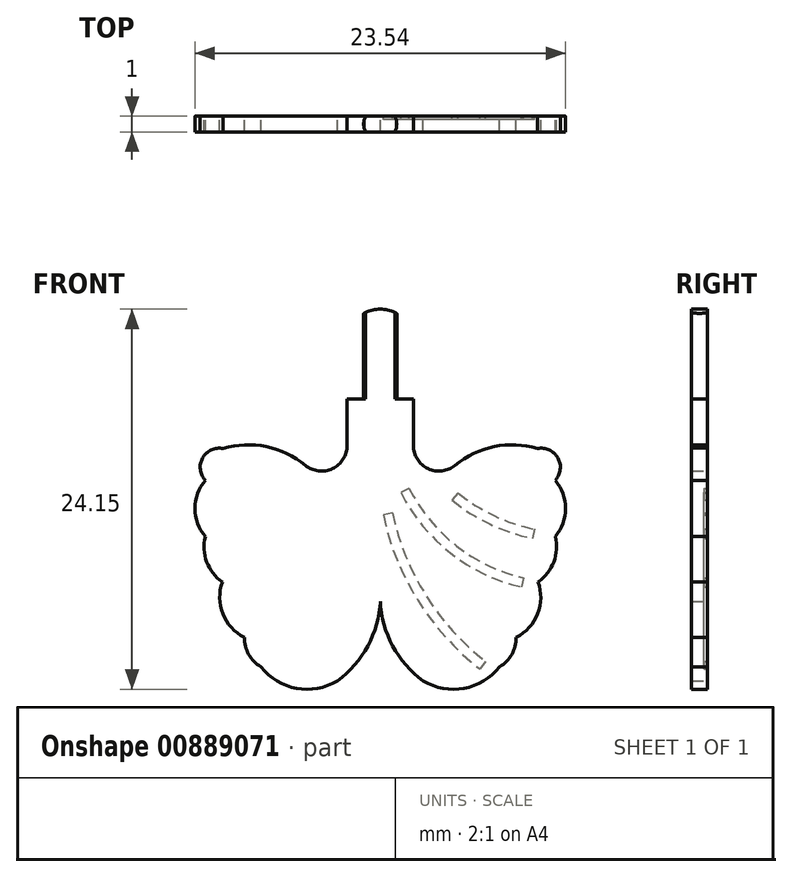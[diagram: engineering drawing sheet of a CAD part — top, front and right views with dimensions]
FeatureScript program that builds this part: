
annotation { "Feature Type Name" : "Feature", "Feature Type Description" : "" }
export const myFeature = defineFeature(function(context is Context, id is Id, definition is map)
    precondition{}
    {
        {
            var Q0;
            Q0=qCreatedBy(makeId("Front.planeOp"),FACE);
            var sketch = newSketch(context, id + "F0", { "sketchPlane" : qUnion([Q0])});
            skLineSegment(sketch, "E0", {"start": v(0, 4.31) * mm, "end": v(0, 0) * mm, "construction": true});
            skLineSegment(sketch, "E1", {"start": v(6, 0) * mm, "end": v(0, 0) * mm, "construction": true});
            skLineSegment(sketch, "E2", {"start": v(1.05, 6.95) * mm, "end": v(1.05, 3.67) * mm});
            skArc(sketch, "E3", {"start": v(0, -1.28) * mm, "mid": v(0.4, -2.7) * mm, "end": v(1.36, -3.8) * mm});
            skArc(sketch, "E4", {"start": v(1.36, -3.8) * mm, "mid": v(2.66, -4.05) * mm, "end": v(3.79, -3.36) * mm});
            skArc(sketch, "E5", {"start": v(3.79, -3.36) * mm, "mid": v(4.18, -2.97) * mm, "end": v(4.31, -2.43) * mm});
            skArc(sketch, "E6", {"start": v(4.31, -2.43) * mm, "mid": v(5, -1.68) * mm, "end": v(5.01, -0.66) * mm});
            skArc(sketch, "E7", {"start": v(5.01, -0.66) * mm, "mid": v(5.51, -0.03) * mm, "end": v(5.56, 0.77) * mm});
            skArc(sketch, "E8", {"start": v(5.56, 0.77) * mm, "mid": v(5.88, 1.67) * mm, "end": v(5.56, 2.56) * mm});
            skArc(sketch, "E9", {"start": v(1.05, 3.67) * mm, "mid": v(1.52, 2.93) * mm, "end": v(2.38, 3.04) * mm});
            skArc(sketch, "E10", {"start": v(5.56, 2.56) * mm, "mid": v(5.64, 3.27) * mm, "end": v(5, 3.57) * mm});
            skArc(sketch, "E11", {"start": v(5, 3.57) * mm, "mid": v(3.62, 3.63) * mm, "end": v(2.38, 3.04) * mm});
            skLineSegment(sketch, "E12.left", {"start": v(1.05, 6.95) * mm, "end": v(1.05, 6.95) * mm});
            skLineSegment(sketch, "E12.right", {"start": v(0, 6.95) * mm, "end": v(0, 6.95) * mm});
            skLineSegment(sketch, "E13.bottom", {"start": v(0, -1.28) * mm, "end": v(0, -1.28) * mm});
            skLineSegment(sketch, "E13.left", {"start": v(0, -1.28) * mm, "end": v(0, 8) * mm});
            skLineSegment(sketch, "E13.right", {"start": v(0, -1.28) * mm, "end": v(0, 6.95) * mm});
            skArc(sketch, "E14", {"start": v(1.05, 6.95) * mm, "mid": v(0.74, 7.7) * mm, "end": v(0, 8) * mm});
            skSolve(sketch);
        }
        {
            var Q0;
            Q0=makeQuery(id+"F0.imprint","IMPRINT",FACE,{"disambiguationData":[TD([[makeQuery(id+"F0.imprint","IMPRINT",EDGE,{"derivedFrom":sQuery(id+"F0.wireOp",EDGE,"E2")}),-1.0]])]});
            extrude(context, id + "F1", {"entities" : qUnion([Q0]), "depth" : .25 * mm, "offsetDistance" : 25 * mm, "hasSecondDirection" : true, "secondDirectionOppositeDirection" : true, "secondDirectionDepth" : .25 * mm});
        }
        {
            var Q0;
            Q0=makeQuery(id+"F1.opExtrude","SWEPT_BODY",BODY,{"disambiguationData":[OSD([sQuery(id+"F0.wireOp",EDGE,"E2"),sQuery(id+"F0.wireOp",EDGE,"E3"),sQuery(id+"F0.wireOp",EDGE,"E4"),sQuery(id+"F0.wireOp",EDGE,"E5"),sQuery(id+"F0.wireOp",EDGE,"E6"),sQuery(id+"F0.wireOp",EDGE,"E7"),sQuery(id+"F0.wireOp",EDGE,"E8"),sQuery(id+"F0.wireOp",EDGE,"E9"),sQuery(id+"F0.wireOp",EDGE,"E10"),sQuery(id+"F0.wireOp",EDGE,"E11"),sQuery(id+"F0.wireOp",EDGE,"E13.left"),sQuery(id+"F0.wireOp",EDGE,"E13.right"),sQuery(id+"F0.wireOp",EDGE,"E14")])]});
            var Q1;
            Q1=makeQuery(id+"F1.opExtrude","SWEPT_FACE",FACE,{"disambiguationData":[OSD([sQuery(id+"F0.wireOp",EDGE,"E13.left"),sQuery(id+"F0.wireOp",EDGE,"E13.right")])]});
            mirror(context, id + "F2", {"operationType" : NewBodyOperationType.ADD, "entities" : qUnion([Q0]), "mirrorPlane" : qUnion([Q1])});
        }
        {
            var Q0;
            Q0=qCreatedBy(makeId("Top.planeOp"),FACE);
            cPlane(context, id + "F3", {"entities" : qUnion([Q0]), "cplaneType" : CPlaneType.OFFSET, "offset" : 20 * mm, "width" : 150 * mm, "height" : 150 * mm});
        }
        {
            var Q0;
            Q0=qCreatedBy(id+"F3.planeOp",FACE);
            var sketch = newSketch(context, id + "F4", { "sketchPlane" : qUnion([Q0])});
            skCircle(sketch, "E15", {"center": v(0, 0) * mm, "radius": 1.05 * mm});
            skCircle(sketch, "E16", {"center": v(0, 0) * mm, "radius": 3 * mm});
            skSolve(sketch);
        }
        {
            var Q0;
            {var subQ0=makeQuery(id+"F1.opExtrude","CAP_FACE",FACE,{"disambiguationData":[OSD([sQuery(id+"F0.wireOp",EDGE,"E2"),sQuery(id+"F0.wireOp",EDGE,"E3"),sQuery(id+"F0.wireOp",EDGE,"E4"),sQuery(id+"F0.wireOp",EDGE,"E5"),sQuery(id+"F0.wireOp",EDGE,"E6"),sQuery(id+"F0.wireOp",EDGE,"E7"),sQuery(id+"F0.wireOp",EDGE,"E8"),sQuery(id+"F0.wireOp",EDGE,"E9"),sQuery(id+"F0.wireOp",EDGE,"E10"),sQuery(id+"F0.wireOp",EDGE,"E11"),sQuery(id+"F0.wireOp",EDGE,"E13.left"),sQuery(id+"F0.wireOp",EDGE,"E13.right"),sQuery(id+"F0.wireOp",EDGE,"E14")])],"isStart":true});Q0=makeQuery(id+"F2.boolean.opBoolean","MERGE",FACE,{"derivedFrom":[subQ0,makeQuery(id+"F2.opPattern","COPY",FACE,{"derivedFrom":subQ0,"instanceName":"1"})]});}
            var sketch = newSketch(context, id + "F5", { "sketchPlane" : qUnion([Q0])});
            skArc(sketch, "E17", {"start": v(-3.34, -3.19) * mm, "mid": v(-1.45, -1.1) * mm, "end": v(-0.39, 1.52) * mm});
            skArc(sketch, "E18", {"start": v(-4.54, -0.53) * mm, "mid": v(-2.42, 0.48) * mm, "end": v(-0.92, 2.3) * mm});
            skArc(sketch, "E19", {"start": v(-4.9, 1.01) * mm, "mid": v(-3.6, 1.44) * mm, "end": v(-2.47, 2.17) * mm});
            skArc(sketch, "E20.0", {"start": v(-4.83, 0.72) * mm, "mid": v(-3.48, 1.17) * mm, "end": v(-2.28, 1.94) * mm});
            skArc(sketch, "E21.0", {"start": v(-4.48, -0.83) * mm, "mid": v(-2.23, 0.25) * mm, "end": v(-0.65, 2.17) * mm});
            skArc(sketch, "E22.0", {"start": v(-3.16, -3.43) * mm, "mid": v(-1.2, -1.25) * mm, "end": v(-0.1, 1.46) * mm});
            skLineSegment(sketch, "E23", {"start": v(-4.9, 1.01) * mm, "end": v(-4.83, 0.72) * mm});
            skLineSegment(sketch, "E24", {"start": v(-4.54, -0.53) * mm, "end": v(-4.48, -0.83) * mm});
            skLineSegment(sketch, "E25", {"start": v(-3.34, -3.19) * mm, "end": v(-3.16, -3.43) * mm});
            skLineSegment(sketch, "E26", {"start": v(-2.47, 2.17) * mm, "end": v(-2.28, 1.94) * mm});
            skLineSegment(sketch, "E27", {"start": v(-0.92, 2.3) * mm, "end": v(-0.65, 2.17) * mm});
            skLineSegment(sketch, "E28", {"start": v(-0.39, 1.52) * mm, "end": v(-0.1, 1.46) * mm});
            skSolve(sketch);
        }
        {
            var Q0;
            Q0=makeQuery(id+"F5.imprint","IMPRINT",FACE,{"disambiguationData":[TD([[makeQuery(id+"F5.imprint","IMPRINT",EDGE,{"derivedFrom":sQuery(id+"F5.wireOp",EDGE,"E19")}),-1.0]])]});
            var Q1;
            Q1=makeQuery(id+"F5.imprint","IMPRINT",FACE,{"disambiguationData":[TD([[makeQuery(id+"F5.imprint","IMPRINT",EDGE,{"derivedFrom":sQuery(id+"F5.wireOp",EDGE,"E18")}),-1.0]])]});
            var Q2;
            Q2=makeQuery(id+"F5.imprint","IMPRINT",FACE,{"disambiguationData":[TD([[makeQuery(id+"F5.imprint","IMPRINT",EDGE,{"derivedFrom":sQuery(id+"F5.wireOp",EDGE,"E17")}),-1.0]])]});
            extrude(context, id + "F6", {"entities" : qUnion([Q0, Q1, Q2]), "operationType" : NewBodyOperationType.REMOVE, "oppositeDirection" : true, "depth" : .1 * mm, "offsetDistance" : 25 * mm});
        }
        {
            var Q0;
            Q0=makeQuery(id+"F1.opExtrude","SWEPT_BODY",BODY,{"disambiguationData":[OSD([sQuery(id+"F0.wireOp",EDGE,"E2"),sQuery(id+"F0.wireOp",EDGE,"E3"),sQuery(id+"F0.wireOp",EDGE,"E4"),sQuery(id+"F0.wireOp",EDGE,"E5"),sQuery(id+"F0.wireOp",EDGE,"E6"),sQuery(id+"F0.wireOp",EDGE,"E7"),sQuery(id+"F0.wireOp",EDGE,"E8"),sQuery(id+"F0.wireOp",EDGE,"E9"),sQuery(id+"F0.wireOp",EDGE,"E10"),sQuery(id+"F0.wireOp",EDGE,"E11"),sQuery(id+"F0.wireOp",EDGE,"E13.left"),sQuery(id+"F0.wireOp",EDGE,"E13.right"),sQuery(id+"F0.wireOp",EDGE,"E14")])]});
            var Q1;
            Q1=qCreatedBy(makeId("Origin.pointOp"),VERTEX);
            transform(context, id + "F7", {"entities" : qUnion([Q0]), "transformType" : TransformType.SCALE_UNIFORMLY, "scale" : 2, "scalePoint" : qUnion([Q1]), "makeCopy" : false});
        }
        {
            var Q0;
            Q0=makeQuery(id+"F4.imprint","IMPRINT",FACE,{"disambiguationData":[TD([[makeQuery(id+"F4.imprint","IMPRINT",EDGE,{"derivedFrom":sQuery(id+"F4.wireOp",EDGE,"E15")}),-1.0]])]});
            extrude(context, id + "F8", {"entities" : qUnion([Q0]), "operationType" : NewBodyOperationType.REMOVE, "oppositeDirection" : true, "depth" : 9.7 * mm, "offsetDistance" : 25 * mm});
        }
    });
